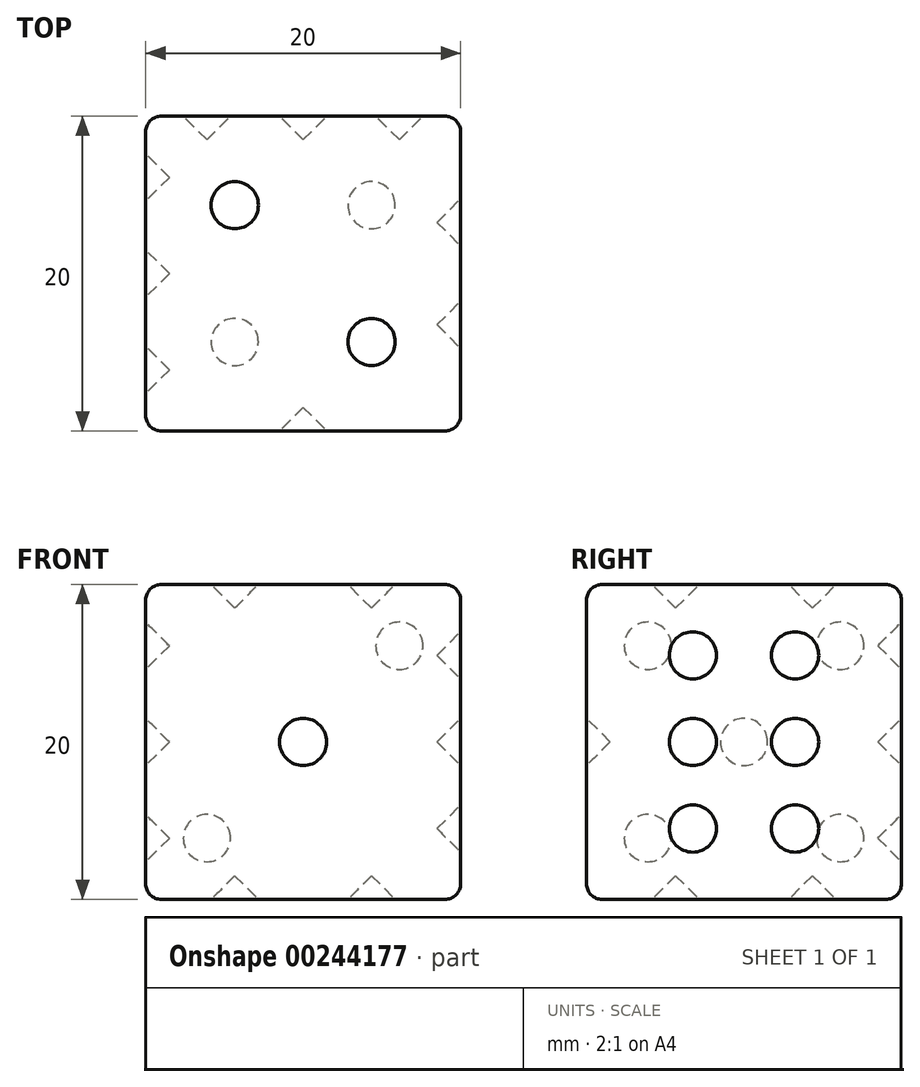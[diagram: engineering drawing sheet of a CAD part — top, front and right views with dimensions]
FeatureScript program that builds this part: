
annotation { "Feature Type Name" : "Feature", "Feature Type Description" : "" }
export const myFeature = defineFeature(function(context is Context, id is Id, definition is map)
    precondition{}
    {
        {
            var Q0;
            Q0=qCreatedBy(makeId("Top.planeOp"),FACE);
            var sketch = newSketch(context, id + "F0", { "sketchPlane" : qUnion([Q0])});
            skLineSegment(sketch, "E0.bottom", {"start": v(0, 0) * mm, "end": v(20, 0) * mm});
            skLineSegment(sketch, "E0.top", {"start": v(0, 20) * mm, "end": v(20, 20) * mm});
            skLineSegment(sketch, "E0.left", {"start": v(0, 0) * mm, "end": v(0, 20) * mm});
            skLineSegment(sketch, "E0.right", {"start": v(20, 0) * mm, "end": v(20, 20) * mm});
            skSolve(sketch);
        }
        {
            var Q0;
            Q0 = qSketchRegion(id + "F0", true);
            extrude(context, id + "F1", {"entities" : qUnion([Q0]), "depth" : 20 * mm});
        }
        {
            var Q0;
            Q0=makeQuery(id+"F1.opExtrude","SWEPT_FACE",FACE,{"disambiguationData":[OSD([sQuery(id+"F0.wireOp",EDGE,"E0.bottom")])]});
            var sketch = newSketch(context, id + "F2", { "sketchPlane" : qUnion([Q0])});
            skLineSegment(sketch, "E1", {"start": v(10, 20) * mm, "end": v(10, 0) * mm, "construction": true});
            skCircle(sketch, "E2", {"center": v(10, 10) * mm, "radius": 1.5 * mm});
            skSolve(sketch);
        }
        {
            var Q0;
            Q0 = qSketchRegion(id + "F2", true);
            extrude(context, id + "F3", {"entities" : qUnion([Q0]), "operationType" : NewBodyOperationType.REMOVE, "oppositeDirection" : true, "depth" : 1.5 * mm});
        }
        {
            var Q0;
            Q0=makeQuery(id+"F1.opExtrude","CAP_FACE",FACE,{"disambiguationData":[OSD([sQuery(id+"F0.wireOp",EDGE,"E0.bottom"),sQuery(id+"F0.wireOp",EDGE,"E0.top"),sQuery(id+"F0.wireOp",EDGE,"E0.left"),sQuery(id+"F0.wireOp",EDGE,"E0.right")])],"isStart":false});
            var sketch = newSketch(context, id + "F4", { "sketchPlane" : qUnion([Q0])});
            skLineSegment(sketch, "E3", {"start": v(20, 0) * mm, "end": v(14.34, 5.66) * mm, "construction": true});
            skLineSegment(sketch, "E4", {"start": v(0, 20) * mm, "end": v(5.66, 14.34) * mm, "construction": true});
            skCircle(sketch, "E5", {"center": v(5.66, 14.34) * mm, "radius": 1.5 * mm});
            skCircle(sketch, "E6", {"center": v(14.34, 5.66) * mm, "radius": 1.5 * mm});
            skSolve(sketch);
        }
        {
            var Q0;
            Q0=makeQuery(id+"F4.imprint","IMPRINT",FACE,{"disambiguationData":[TD([[makeQuery(id+"F4.imprint","IMPRINT",EDGE,{"derivedFrom":sQuery(id+"F4.wireOp",EDGE,"E5")}),1.0]])]});
            var Q1;
            Q1=makeQuery(id+"F4.imprint","IMPRINT",FACE,{"disambiguationData":[TD([[makeQuery(id+"F4.imprint","IMPRINT",EDGE,{"derivedFrom":sQuery(id+"F4.wireOp",EDGE,"E6")}),1.0]])]});
            var Q2;
            Q2=sQuery(id+"F4.wireOp",EDGE,"E5");
            var Q3;
            Q3=sQuery(id+"F4.wireOp",EDGE,"E6");
            extrude(context, id + "F5", {"entities" : qUnion([Q0, Q1]), "operationType" : NewBodyOperationType.REMOVE, "surfaceEntities" : qUnion([Q2, Q3]), "oppositeDirection" : true, "depth" : 1.5 * mm});
        }
        {
            var Q0;
            Q0=makeQuery(id+"F5.boolean.opBoolean","COPY",FACE,{"derivedFrom":makeQuery(id+"F5.opExtrude","CAP_FACE",FACE,{"disambiguationData":[OSD([sQuery(id+"F4.wireOp",EDGE,"E6")])],"isStart":false})});
            var Q1;
            Q1=makeQuery(id+"F5.boolean.opBoolean","COPY",FACE,{"derivedFrom":makeQuery(id+"F5.opExtrude","CAP_FACE",FACE,{"disambiguationData":[OSD([sQuery(id+"F4.wireOp",EDGE,"E5")])],"isStart":false})});
            chamfer(context, id + "F6", {"entities" : qUnion([Q0, Q1]), "width" : 1.5 * mm, "tangentPropagation" : true});
        }
        {
            var Q0;
            Q0=makeQuery(id+"F3.boolean.opBoolean","COPY",FACE,{"derivedFrom":makeQuery(id+"F3.opExtrude","CAP_FACE",FACE,{"disambiguationData":[OSD([sQuery(id+"F2.wireOp",EDGE,"E2")])],"isStart":false})});
            chamfer(context, id + "F7", {"entities" : qUnion([Q0]), "width" : 1.5 * mm, "tangentPropagation" : true});
        }
        {
            var Q0;
            Q0=makeQuery(id+"F1.opExtrude","SWEPT_FACE",FACE,{"disambiguationData":[OSD([sQuery(id+"F0.wireOp",EDGE,"E0.top")])]});
            var sketch = newSketch(context, id + "F8", { "sketchPlane" : qUnion([Q0])});
            skCircle(sketch, "E7", {"center": v(-10, 10) * mm, "radius": 1.5 * mm});
            skCircle(sketch, "E8", {"center": v(-16.11, 16.11) * mm, "radius": 1.5 * mm});
            skCircle(sketch, "E9", {"center": v(-3.89, 3.89) * mm, "radius": 1.5 * mm});
            skSolve(sketch);
        }
        {
            var Q0;
            Q0=makeQuery(id+"F8.imprint","IMPRINT",FACE,{"disambiguationData":[TD([[makeQuery(id+"F8.imprint","IMPRINT",EDGE,{"derivedFrom":sQuery(id+"F8.wireOp",EDGE,"E8")}),1.0]])]});
            var Q1;
            Q1=makeQuery(id+"F8.imprint","IMPRINT",FACE,{"disambiguationData":[TD([[makeQuery(id+"F8.imprint","IMPRINT",EDGE,{"derivedFrom":sQuery(id+"F8.wireOp",EDGE,"E7")}),1.0]])]});
            var Q2;
            Q2=makeQuery(id+"F8.imprint","IMPRINT",FACE,{"disambiguationData":[TD([[makeQuery(id+"F8.imprint","IMPRINT",EDGE,{"derivedFrom":sQuery(id+"F8.wireOp",EDGE,"E9")}),1.0]])]});
            extrude(context, id + "F9", {"entities" : qUnion([Q0, Q1, Q2]), "operationType" : NewBodyOperationType.REMOVE, "oppositeDirection" : true, "depth" : 1.5 * mm});
        }
        {
            var Q0;
            Q0=makeQuery(id+"F9.boolean.opBoolean","COPY",FACE,{"derivedFrom":makeQuery(id+"F9.opExtrude","CAP_FACE",FACE,{"disambiguationData":[OSD([sQuery(id+"F8.wireOp",EDGE,"E8")])],"isStart":false})});
            var Q1;
            Q1=makeQuery(id+"F9.boolean.opBoolean","COPY",FACE,{"derivedFrom":makeQuery(id+"F9.opExtrude","CAP_FACE",FACE,{"disambiguationData":[OSD([sQuery(id+"F8.wireOp",EDGE,"E7")])],"isStart":false})});
            var Q2;
            Q2=makeQuery(id+"F9.boolean.opBoolean","COPY",FACE,{"derivedFrom":makeQuery(id+"F9.opExtrude","CAP_FACE",FACE,{"disambiguationData":[OSD([sQuery(id+"F8.wireOp",EDGE,"E9")])],"isStart":false})});
            chamfer(context, id + "F10", {"entities" : qUnion([Q0, Q1, Q2]), "width" : 1.5 * mm, "tangentPropagation" : true});
        }
        {
            var Q0;
            Q0=makeQuery(id+"F1.opExtrude","CAP_FACE",FACE,{"disambiguationData":[OSD([sQuery(id+"F0.wireOp",EDGE,"E0.bottom"),sQuery(id+"F0.wireOp",EDGE,"E0.top"),sQuery(id+"F0.wireOp",EDGE,"E0.left"),sQuery(id+"F0.wireOp",EDGE,"E0.right")])],"isStart":true});
            var sketch = newSketch(context, id + "F11", { "sketchPlane" : qUnion([Q0])});
            skCircle(sketch, "E10", {"center": v(5.66, -5.66) * mm, "radius": 1.5 * mm});
            skCircle(sketch, "E11", {"center": v(14.34, -5.66) * mm, "radius": 1.5 * mm});
            skCircle(sketch, "E12", {"center": v(14.34, -14.34) * mm, "radius": 1.5 * mm});
            skCircle(sketch, "E13", {"center": v(5.66, -14.34) * mm, "radius": 1.5 * mm});
            skSolve(sketch);
        }
        {
            var Q0;
            Q0=makeQuery(id+"F11.imprint","IMPRINT",FACE,{"disambiguationData":[TD([[makeQuery(id+"F11.imprint","IMPRINT",EDGE,{"derivedFrom":sQuery(id+"F11.wireOp",EDGE,"E10")}),1.0]])]});
            var Q1;
            Q1=makeQuery(id+"F11.imprint","IMPRINT",FACE,{"disambiguationData":[TD([[makeQuery(id+"F11.imprint","IMPRINT",EDGE,{"derivedFrom":sQuery(id+"F11.wireOp",EDGE,"E11")}),1.0]])]});
            var Q2;
            Q2=makeQuery(id+"F11.imprint","IMPRINT",FACE,{"disambiguationData":[TD([[makeQuery(id+"F11.imprint","IMPRINT",EDGE,{"derivedFrom":sQuery(id+"F11.wireOp",EDGE,"E12")}),1.0]])]});
            var Q3;
            Q3=makeQuery(id+"F11.imprint","IMPRINT",FACE,{"disambiguationData":[TD([[makeQuery(id+"F11.imprint","IMPRINT",EDGE,{"derivedFrom":sQuery(id+"F11.wireOp",EDGE,"E13")}),1.0]])]});
            var Q4;
            Q4=sQuery(id+"F11.wireOp",EDGE,"E11");
            var Q5;
            Q5=sQuery(id+"F11.wireOp",EDGE,"E10");
            var Q6;
            Q6=sQuery(id+"F11.wireOp",EDGE,"E13");
            var Q7;
            Q7=sQuery(id+"F11.wireOp",EDGE,"E12");
            extrude(context, id + "F12", {"entities" : qUnion([Q0, Q1, Q2, Q3]), "operationType" : NewBodyOperationType.REMOVE, "surfaceEntities" : qUnion([Q4, Q5, Q6, Q7]), "oppositeDirection" : true, "depth" : 1.5 * mm});
        }
        {
            var Q0;
            Q0=makeQuery(id+"F12.boolean.opBoolean","COPY",FACE,{"derivedFrom":makeQuery(id+"F12.opExtrude","CAP_FACE",FACE,{"disambiguationData":[OSD([sQuery(id+"F11.wireOp",EDGE,"E13")])],"isStart":false})});
            var Q1;
            Q1=makeQuery(id+"F12.boolean.opBoolean","COPY",FACE,{"derivedFrom":makeQuery(id+"F12.opExtrude","CAP_FACE",FACE,{"disambiguationData":[OSD([sQuery(id+"F11.wireOp",EDGE,"E10")])],"isStart":false})});
            var Q2;
            Q2=makeQuery(id+"F12.boolean.opBoolean","COPY",FACE,{"derivedFrom":makeQuery(id+"F12.opExtrude","CAP_FACE",FACE,{"disambiguationData":[OSD([sQuery(id+"F11.wireOp",EDGE,"E11")])],"isStart":false})});
            var Q3;
            Q3=makeQuery(id+"F12.boolean.opBoolean","COPY",FACE,{"derivedFrom":makeQuery(id+"F12.opExtrude","CAP_FACE",FACE,{"disambiguationData":[OSD([sQuery(id+"F11.wireOp",EDGE,"E12")])],"isStart":false})});
            chamfer(context, id + "F13", {"entities" : qUnion([Q0, Q1, Q2, Q3]), "width" : 1.5 * mm, "tangentPropagation" : true});
        }
        {
            var Q0;
            Q0=makeQuery(id+"F1.opExtrude","SWEPT_FACE",FACE,{"disambiguationData":[OSD([sQuery(id+"F0.wireOp",EDGE,"E0.left")])]});
            var sketch = newSketch(context, id + "F14", { "sketchPlane" : qUnion([Q0])});
            skCircle(sketch, "E14", {"center": v(-10, 10) * mm, "radius": 1.5 * mm});
            skCircle(sketch, "E15", {"center": v(-16.11, 16.11) * mm, "radius": 1.5 * mm});
            skCircle(sketch, "E16", {"center": v(-3.89, 16.11) * mm, "radius": 1.5 * mm});
            skCircle(sketch, "E17", {"center": v(-3.89, 3.89) * mm, "radius": 1.5 * mm});
            skCircle(sketch, "E18", {"center": v(-16.11, 3.89) * mm, "radius": 1.5 * mm});
            skSolve(sketch);
        }
        {
            var Q0;
            Q0=makeQuery(id+"F14.imprint","IMPRINT",FACE,{"disambiguationData":[TD([[makeQuery(id+"F14.imprint","IMPRINT",EDGE,{"derivedFrom":sQuery(id+"F14.wireOp",EDGE,"E15")}),1.0]])]});
            var Q1;
            Q1=makeQuery(id+"F14.imprint","IMPRINT",FACE,{"disambiguationData":[TD([[makeQuery(id+"F14.imprint","IMPRINT",EDGE,{"derivedFrom":sQuery(id+"F14.wireOp",EDGE,"E16")}),1.0]])]});
            var Q2;
            Q2=makeQuery(id+"F14.imprint","IMPRINT",FACE,{"disambiguationData":[TD([[makeQuery(id+"F14.imprint","IMPRINT",EDGE,{"derivedFrom":sQuery(id+"F14.wireOp",EDGE,"E14")}),1.0]])]});
            var Q3;
            Q3=makeQuery(id+"F14.imprint","IMPRINT",FACE,{"disambiguationData":[TD([[makeQuery(id+"F14.imprint","IMPRINT",EDGE,{"derivedFrom":sQuery(id+"F14.wireOp",EDGE,"E18")}),1.0]])]});
            var Q4;
            Q4=makeQuery(id+"F14.imprint","IMPRINT",FACE,{"disambiguationData":[TD([[makeQuery(id+"F14.imprint","IMPRINT",EDGE,{"derivedFrom":sQuery(id+"F14.wireOp",EDGE,"E17")}),1.0]])]});
            extrude(context, id + "F15", {"entities" : qUnion([Q0, Q1, Q2, Q3, Q4]), "operationType" : NewBodyOperationType.REMOVE, "oppositeDirection" : true, "depth" : 1.5 * mm});
        }
        {
            var Q0;
            Q0=makeQuery(id+"F15.boolean.opBoolean","COPY",FACE,{"derivedFrom":makeQuery(id+"F15.opExtrude","CAP_FACE",FACE,{"disambiguationData":[OSD([sQuery(id+"F14.wireOp",EDGE,"E15")])],"isStart":false})});
            var Q1;
            Q1=makeQuery(id+"F15.boolean.opBoolean","COPY",EDGE,{"derivedFrom":makeQuery(id+"F15.opExtrude","CAP_EDGE",EDGE,{"disambiguationData":[OSD([sQuery(id+"F14.wireOp",EDGE,"E16")])],"isStart":false})});
            var Q2;
            Q2=makeQuery(id+"F15.boolean.opBoolean","COPY",EDGE,{"derivedFrom":makeQuery(id+"F15.opExtrude","CAP_EDGE",EDGE,{"disambiguationData":[OSD([sQuery(id+"F14.wireOp",EDGE,"E14")])],"isStart":false})});
            var Q3;
            Q3=makeQuery(id+"F15.boolean.opBoolean","COPY",FACE,{"derivedFrom":makeQuery(id+"F15.opExtrude","CAP_FACE",FACE,{"disambiguationData":[OSD([sQuery(id+"F14.wireOp",EDGE,"E17")])],"isStart":false})});
            var Q4;
            Q4=makeQuery(id+"F15.boolean.opBoolean","COPY",FACE,{"derivedFrom":makeQuery(id+"F15.opExtrude","CAP_FACE",FACE,{"disambiguationData":[OSD([sQuery(id+"F14.wireOp",EDGE,"E18")])],"isStart":false})});
            chamfer(context, id + "F16", {"entities" : qUnion([Q0, Q1, Q2, Q3, Q4]), "width" : 1.5 * mm, "tangentPropagation" : true});
        }
        {
            var Q0;
            Q0=makeQuery(id+"F1.opExtrude","SWEPT_FACE",FACE,{"disambiguationData":[OSD([sQuery(id+"F0.wireOp",EDGE,"E0.right")])]});
            var sketch = newSketch(context, id + "F17", { "sketchPlane" : qUnion([Q0])});
            skCircle(sketch, "E19", {"center": v(6.75, 15.5) * mm, "radius": 1.5 * mm});
            skCircle(sketch, "E20", {"center": v(13.25, 4.5) * mm, "radius": 1.5 * mm});
            skCircle(sketch, "E21", {"center": v(6.75, 4.5) * mm, "radius": 1.5 * mm});
            skLineSegment(sketch, "E22", {"start": v(0, 10) * mm, "end": v(20, 10) * mm, "construction": true});
            skLineSegment(sketch, "E23", {"start": v(10, 20) * mm, "end": v(10, 0) * mm, "construction": true});
            skCircle(sketch, "E24", {"center": v(13.25, 15.5) * mm, "radius": 1.5 * mm});
            skCircle(sketch, "E25", {"center": v(13.25, 10) * mm, "radius": 1.5 * mm});
            skCircle(sketch, "E26", {"center": v(6.75, 10) * mm, "radius": 1.5 * mm});
            skSolve(sketch);
        }
        {
            var Q0;
            Q0 = qSketchRegion(id + "F17", true);
            extrude(context, id + "F18", {"entities" : qUnion([Q0]), "operationType" : NewBodyOperationType.REMOVE, "oppositeDirection" : true, "depth" : 1.5 * mm});
        }
        {
            var Q0;
            Q0=makeQuery(id+"F18.boolean.opBoolean","COPY",FACE,{"derivedFrom":makeQuery(id+"F18.opExtrude","CAP_FACE",FACE,{"disambiguationData":[OSD([sQuery(id+"F17.wireOp",EDGE,"E19")])],"isStart":false})});
            var Q1;
            Q1=makeQuery(id+"F18.boolean.opBoolean","COPY",FACE,{"derivedFrom":makeQuery(id+"F18.opExtrude","CAP_FACE",FACE,{"disambiguationData":[OSD([sQuery(id+"F17.wireOp",EDGE,"E24")])],"isStart":false})});
            var Q2;
            Q2=makeQuery(id+"F18.boolean.opBoolean","COPY",FACE,{"derivedFrom":makeQuery(id+"F18.opExtrude","CAP_FACE",FACE,{"disambiguationData":[OSD([sQuery(id+"F17.wireOp",EDGE,"E26")])],"isStart":false})});
            var Q3;
            Q3=makeQuery(id+"F18.boolean.opBoolean","COPY",FACE,{"derivedFrom":makeQuery(id+"F18.opExtrude","CAP_FACE",FACE,{"disambiguationData":[OSD([sQuery(id+"F17.wireOp",EDGE,"E25")])],"isStart":false})});
            var Q4;
            Q4=makeQuery(id+"F18.boolean.opBoolean","COPY",FACE,{"derivedFrom":makeQuery(id+"F18.opExtrude","CAP_FACE",FACE,{"disambiguationData":[OSD([sQuery(id+"F17.wireOp",EDGE,"E20")])],"isStart":false})});
            var Q5;
            Q5=makeQuery(id+"F18.boolean.opBoolean","COPY",FACE,{"derivedFrom":makeQuery(id+"F18.opExtrude","CAP_FACE",FACE,{"disambiguationData":[OSD([sQuery(id+"F17.wireOp",EDGE,"E21")])],"isStart":false})});
            chamfer(context, id + "F19", {"entities" : qUnion([Q0, Q1, Q2, Q3, Q4, Q5]), "width" : 1.5 * mm, "tangentPropagation" : true});
        }
        {
            var Q0;
            Q0=makeQuery(id+"F1.opExtrude","CAP_EDGE",EDGE,{"disambiguationData":[OSD([sQuery(id+"F0.wireOp",EDGE,"E0.top")])],"isStart":false});
            var Q1;
            Q1=makeQuery(id+"F1.opExtrude","CAP_EDGE",EDGE,{"disambiguationData":[OSD([sQuery(id+"F0.wireOp",EDGE,"E0.right")])],"isStart":false});
            var Q2;
            Q2=makeQuery(id+"F1.opExtrude","CAP_EDGE",EDGE,{"disambiguationData":[OSD([sQuery(id+"F0.wireOp",EDGE,"E0.left")])],"isStart":false});
            var Q3;
            Q3=makeQuery(id+"F1.opExtrude","CAP_EDGE",EDGE,{"disambiguationData":[OSD([sQuery(id+"F0.wireOp",EDGE,"E0.bottom")])],"isStart":false});
            var Q4;
            Q4=makeQuery(id+"F1.opExtrude","SWEPT_EDGE",EDGE,{"disambiguationData":[OSD([sQuery(id+"F0.wireOp",EDGE,"E0.top"),sQuery(id+"F0.wireOp",EDGE,"E0.left")])]});
            var Q5;
            Q5=makeQuery(id+"F1.opExtrude","CAP_EDGE",EDGE,{"disambiguationData":[OSD([sQuery(id+"F0.wireOp",EDGE,"E0.left")])],"isStart":true});
            var Q6;
            Q6=makeQuery(id+"F1.opExtrude","CAP_EDGE",EDGE,{"disambiguationData":[OSD([sQuery(id+"F0.wireOp",EDGE,"E0.top")])],"isStart":true});
            var Q7;
            Q7=makeQuery(id+"F1.opExtrude","SWEPT_EDGE",EDGE,{"disambiguationData":[OSD([sQuery(id+"F0.wireOp",EDGE,"E0.top"),sQuery(id+"F0.wireOp",EDGE,"E0.right")])]});
            var Q8;
            Q8=makeQuery(id+"F1.opExtrude","SWEPT_EDGE",EDGE,{"disambiguationData":[OSD([sQuery(id+"F0.wireOp",EDGE,"E0.bottom"),sQuery(id+"F0.wireOp",EDGE,"E0.left")])]});
            var Q9;
            Q9=makeQuery(id+"F1.opExtrude","CAP_EDGE",EDGE,{"disambiguationData":[OSD([sQuery(id+"F0.wireOp",EDGE,"E0.bottom")])],"isStart":true});
            var Q10;
            Q10=makeQuery(id+"F1.opExtrude","SWEPT_EDGE",EDGE,{"disambiguationData":[OSD([sQuery(id+"F0.wireOp",EDGE,"E0.bottom"),sQuery(id+"F0.wireOp",EDGE,"E0.right")])]});
            var Q11;
            Q11=makeQuery(id+"F1.opExtrude","CAP_EDGE",EDGE,{"disambiguationData":[OSD([sQuery(id+"F0.wireOp",EDGE,"E0.right")])],"isStart":true});
            fillet(context, id + "F20", {"entities" : qUnion([Q0, Q1, Q2, Q3, Q4, Q5, Q6, Q7, Q8, Q9, Q10, Q11]), "radius" : 1 * mm, "tangentPropagation" : true, "allowEdgeOverflow" : false});
        }
    });
